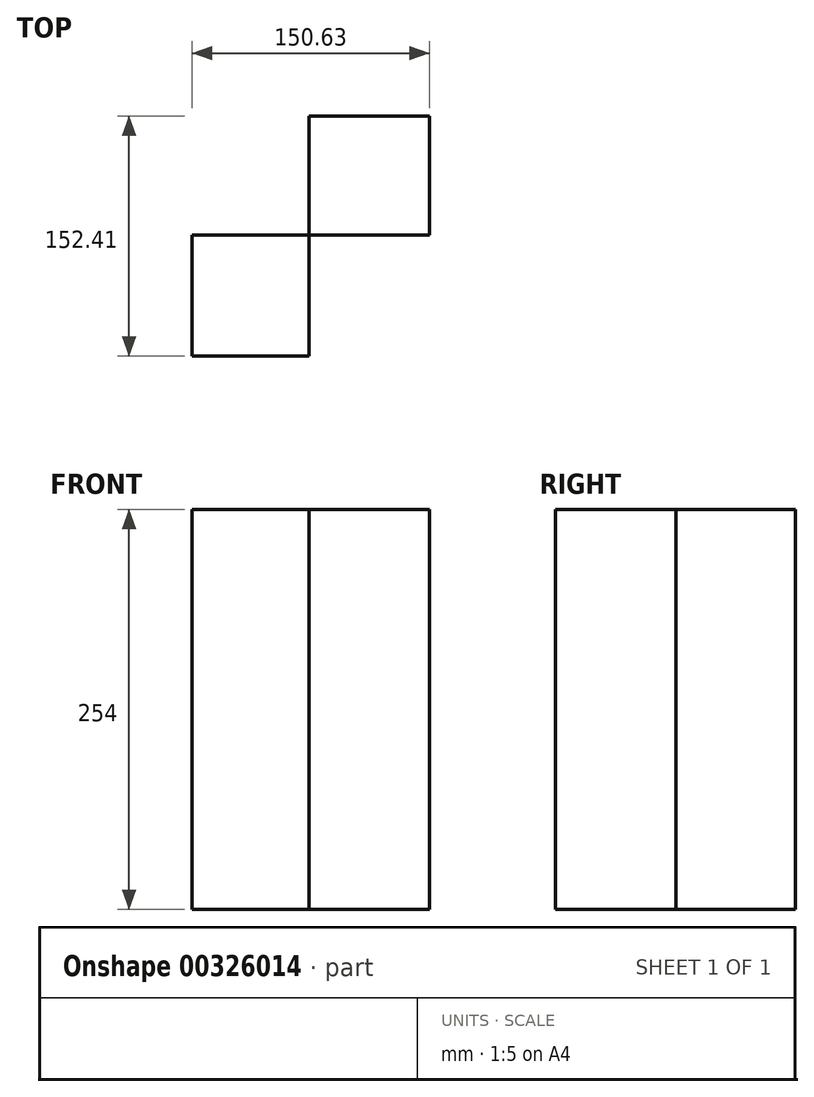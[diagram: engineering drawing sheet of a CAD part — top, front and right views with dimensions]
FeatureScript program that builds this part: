
annotation { "Feature Type Name" : "Feature", "Feature Type Description" : "" }
export const myFeature = defineFeature(function(context is Context, id is Id, definition is map)
    precondition{}
    {
        {
            var Q0;
            Q0=qCreatedBy(makeId("Top.planeOp"),FACE);
            var sketch = newSketch(context, id + "F0", { "sketchPlane" : qUnion([Q0])});
            skLineSegment(sketch, "E0.bottom", {"start": v(0, 0) * mm, "end": v(76.32, 0) * mm});
            skLineSegment(sketch, "E0.top", {"start": v(0, 75.63) * mm, "end": v(76.32, 75.63) * mm});
            skLineSegment(sketch, "E0.left", {"start": v(0, 0) * mm, "end": v(0, 75.63) * mm});
            skLineSegment(sketch, "E0.right", {"start": v(76.32, 0) * mm, "end": v(76.32, 75.63) * mm});
            skLineSegment(sketch, "E1.bottom", {"start": v(0, 0) * mm, "end": v(-74.31, 0) * mm});
            skLineSegment(sketch, "E1.top", {"start": v(0, -76.78) * mm, "end": v(-74.31, -76.78) * mm});
            skLineSegment(sketch, "E1.left", {"start": v(0, 0) * mm, "end": v(0, -76.78) * mm});
            skLineSegment(sketch, "E1.right", {"start": v(-74.31, 0) * mm, "end": v(-74.31, -76.78) * mm});
            skSolve(sketch);
        }
        {
            var Q0;
            Q0 = qSketchRegion(id + "F0", true);
            extrude(context, id + "F1", {"entities" : qUnion([Q0]), "depth" : 254 * mm});
        }
    });
